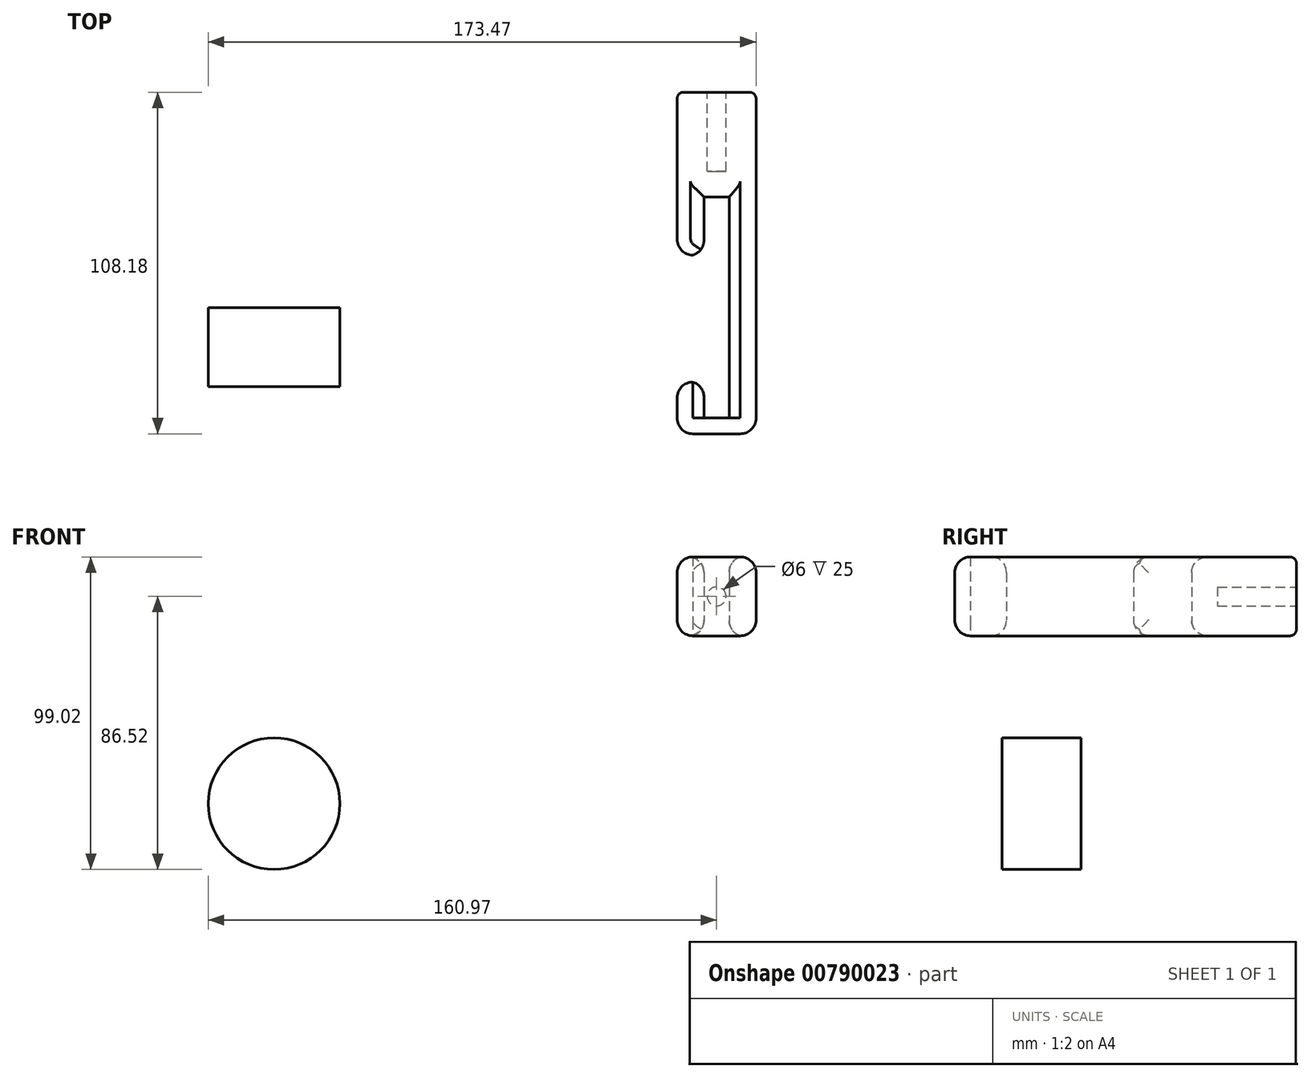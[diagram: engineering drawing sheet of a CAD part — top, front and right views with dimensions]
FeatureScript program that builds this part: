
annotation { "Feature Type Name" : "Feature", "Feature Type Description" : "" }
export const myFeature = defineFeature(function(context is Context, id is Id, definition is map)
    precondition{}
    {
        {
            var Q0;
            Q0=qCreatedBy(makeId("Top.planeOp"),FACE);
            var sketch = newSketch(context, id + "F0", { "sketchPlane" : qUnion([Q0])});
            skLineSegment(sketch, "E0.top", {"start": v(-12.5, -40) * mm, "end": v(12.5, -40) * mm});
            skLineSegment(sketch, "E0.left", {"start": v(-12.5, 40) * mm, "end": v(-12.5, 16.61) * mm});
            skLineSegment(sketch, "E0.right", {"start": v(12.5, 40) * mm, "end": v(12.5, -40) * mm});
            skPoint(sketch, "E0.middle", {"position": v(0, 0) * mm});
            skLineSegment(sketch, "E1.bottom", {"start": v(-4, 35) * mm, "end": v(4, 35) * mm});
            skLineSegment(sketch, "E1.top", {"start": v(-4, -35) * mm, "end": v(4, -35) * mm});
            skLineSegment(sketch, "E1.left", {"start": v(-4, 35) * mm, "end": v(-4, 16.61) * mm});
            skLineSegment(sketch, "E1.right", {"start": v(4, 35) * mm, "end": v(4, -35) * mm});
            skLineSegment(sketch, "E2", {"start": v(-12.5, 16.61) * mm, "end": v(-4, 16.61) * mm});
            skLineSegment(sketch, "E3", {"start": v(-12.5, -23.6) * mm, "end": v(-4, -23.6) * mm});
            skLineSegment(sketch, "E4.trimOffspring", {"start": v(-12.5, -23.6) * mm, "end": v(-12.5, -40) * mm});
            skLineSegment(sketch, "E5.trimOffspring", {"start": v(-4, -23.6) * mm, "end": v(-4, -35) * mm});
            skLineSegment(sketch, "E6.top", {"start": v(-12.5, 68.18) * mm, "end": v(12.5, 68.18) * mm});
            skLineSegment(sketch, "E7", {"start": v(-12.5, 40) * mm, "end": v(-12.5, 68.18) * mm});
            skLineSegment(sketch, "E8", {"start": v(12.5, 40) * mm, "end": v(12.5, 68.18) * mm});
            skSolve(sketch);
        }
        {
            var Q0;
            Q0 = qSketchRegion(id + "F0", true);
            extrude(context, id + "F1", {"entities" : qUnion([Q0]), "depth" : 25 * mm, "offsetDistance" : 25 * mm, "symmetric" : true});
        }
        {
            var Q0;
            Q0=makeQuery(id+"F1.opExtrude","SWEPT_FACE",FACE,{"disambiguationData":[OSD([sQuery(id+"F0.wireOp",EDGE,"E6.top")])]});
            var sketch = newSketch(context, id + "F2", { "sketchPlane" : qUnion([Q0])});
            skCircle(sketch, "E9", {"center": v(0, 0) * mm, "radius": 3 * mm});
            skSolve(sketch);
        }
        {
            var Q0;
            Q0=makeQuery(id+"F2.imprint","IMPRINT",FACE,{"disambiguationData":[TD([[makeQuery(id+"F2.imprint","IMPRINT",EDGE,{"derivedFrom":sQuery(id+"F2.wireOp",EDGE,"E9")}),1.0]])]});
            extrude(context, id + "F3", {"entities" : qUnion([Q0]), "operationType" : NewBodyOperationType.REMOVE, "oppositeDirection" : true, "depth" : 25 * mm, "offsetDistance" : 25 * mm});
        }
        {
            var Q0;
            Q0=makeQuery(id+"F1.opExtrude","SWEPT_EDGE",EDGE,{"disambiguationData":[OSD([sQuery(id+"F0.wireOp",EDGE,"E0.top"),sQuery(id+"F0.wireOp",EDGE,"E4.trimOffspring")])]});
            var Q1;
            Q1=makeQuery(id+"F1.opExtrude","SWEPT_EDGE",EDGE,{"disambiguationData":[OSD([sQuery(id+"F0.wireOp",EDGE,"E0.top"),sQuery(id+"F0.wireOp",EDGE,"E0.right")])]});
            var Q2;
            Q2=makeQuery(id+"F1.opExtrude","SWEPT_EDGE",EDGE,{"disambiguationData":[OSD([sQuery(id+"F0.wireOp",EDGE,"E3"),sQuery(id+"F0.wireOp",EDGE,"E4.trimOffspring")])]});
            var Q3;
            Q3=makeQuery(id+"F1.opExtrude","SWEPT_EDGE",EDGE,{"disambiguationData":[OSD([sQuery(id+"F0.wireOp",EDGE,"E0.left"),sQuery(id+"F0.wireOp",EDGE,"E2")])]});
            fillet(context, id + "F4", {"entities" : qUnion([Q0, Q1, Q2, Q3]), "radius" : 5 * mm, "tangentPropagation" : true, "allowEdgeOverflow" : false});
        }
        {
            var Q0;
            Q0=qCreatedBy(makeId("Front.planeOp"),FACE);
            var sketch = newSketch(context, id + "F5", { "sketchPlane" : qUnion([Q0])});
            skCircle(sketch, "E10", {"center": v(-140.12, -65.67) * mm, "radius": 20.85 * mm});
            skSolve(sketch);
        }
        {
            var Q0;
            Q0=makeQuery(id+"F5.imprint","IMPRINT",FACE,{"disambiguationData":[TD([[makeQuery(id+"F5.imprint","IMPRINT",EDGE,{"derivedFrom":sQuery(id+"F5.wireOp",EDGE,"E10")}),1.0]])]});
            extrude(context, id + "F6", {"entities" : qUnion([Q0]), "depth" : 25 * mm, "offsetDistance" : 25 * mm});
        }
        {
            var Q0;
            Q0=makeQuery(id+"F1.opExtrude","CAP_EDGE",EDGE,{"disambiguationData":[OSD([sQuery(id+"F0.wireOp",EDGE,"E6.top")])],"isStart":true});
            var Q1;
            Q1=makeQuery(id+"F1.opExtrude","SWEPT_EDGE",EDGE,{"disambiguationData":[OSD([sQuery(id+"F0.wireOp",EDGE,"E6.top"),sQuery(id+"F0.wireOp",EDGE,"E7")])]});
            var Q2;
            Q2=makeQuery(id+"F1.opExtrude","SWEPT_EDGE",EDGE,{"disambiguationData":[OSD([sQuery(id+"F0.wireOp",EDGE,"E6.top"),sQuery(id+"F0.wireOp",EDGE,"E8")])]});
            var Q3;
            Q3=makeQuery(id+"F1.opExtrude","CAP_EDGE",EDGE,{"disambiguationData":[OSD([sQuery(id+"F0.wireOp",EDGE,"E6.top")])],"isStart":false});
            fillet(context, id + "F7", {"entities" : qUnion([Q0, Q1, Q2, Q3]), "radius" : 2 * mm, "tangentPropagation" : true, "allowEdgeOverflow" : false});
        }
        {
            var Q0;
            Q0=makeQuery(id+"F1.opExtrude","CAP_EDGE",EDGE,{"disambiguationData":[OSD([sQuery(id+"F0.wireOp",EDGE,"E0.right")])],"isStart":true});
            var Q1;
            Q1=makeQuery(id+"F1.opExtrude","CAP_EDGE",EDGE,{"disambiguationData":[OSD([sQuery(id+"F0.wireOp",EDGE,"E0.right")])],"isStart":false});
            fillet(context, id + "F8", {"entities" : qUnion([Q0, Q1]), "radius" : 5 * mm, "tangentPropagation" : true, "allowEdgeOverflow" : false});
        }
        {
            var Q0;
            Q0=makeQuery(id+"F1.opExtrude","CAP_EDGE",EDGE,{"disambiguationData":[OSD([sQuery(id+"F0.wireOp",EDGE,"E1.left")])],"isStart":true});
            var Q1;
            Q1=makeQuery(id+"F1.opExtrude","CAP_EDGE",EDGE,{"disambiguationData":[OSD([sQuery(id+"F0.wireOp",EDGE,"E1.left")])],"isStart":false});
            var Q2;
            Q2=makeQuery(id+"F1.opExtrude","SWEPT_EDGE",EDGE,{"disambiguationData":[OSD([sQuery(id+"F0.wireOp",EDGE,"E1.left"),sQuery(id+"F0.wireOp",EDGE,"E2")])]});
            var Q3;
            Q3=makeQuery(id+"F1.opExtrude","SWEPT_EDGE",EDGE,{"disambiguationData":[OSD([sQuery(id+"F0.wireOp",EDGE,"E3"),sQuery(id+"F0.wireOp",EDGE,"E5.trimOffspring")])]});
            fillet(context, id + "F9", {"entities" : qUnion([Q0, Q1, Q2, Q3]), "radius" : 5 * mm, "tangentPropagation" : true, "allowEdgeOverflow" : false});
        }
        {
            var Q0;
            Q0=makeQuery(id+"F1.opExtrude","CAP_EDGE",EDGE,{"disambiguationData":[OSD([sQuery(id+"F0.wireOp",EDGE,"E0.left"),sQuery(id+"F0.wireOp",EDGE,"E7")])],"isStart":true});
            var Q1;
            Q1=makeQuery(id+"F1.opExtrude","CAP_EDGE",EDGE,{"disambiguationData":[OSD([sQuery(id+"F0.wireOp",EDGE,"E0.left"),sQuery(id+"F0.wireOp",EDGE,"E7")])],"isStart":false});
            fillet(context, id + "F10", {"entities" : qUnion([Q0, Q1]), "radius" : 5 * mm, "tangentPropagation" : true, "allowEdgeOverflow" : false});
        }
        {
            var Q0;
            Q0=makeQuery(id+"F1.opExtrude","CAP_EDGE",EDGE,{"disambiguationData":[OSD([sQuery(id+"F0.wireOp",EDGE,"E1.bottom")])],"isStart":false});
            var Q1;
            Q1=makeQuery(id+"F1.opExtrude","CAP_EDGE",EDGE,{"disambiguationData":[OSD([sQuery(id+"F0.wireOp",EDGE,"E1.bottom")])],"isStart":true});
            var Q2;
            Q2=makeQuery(id+"F1.opExtrude","CAP_EDGE",EDGE,{"disambiguationData":[OSD([sQuery(id+"F0.wireOp",EDGE,"E1.right")])],"isStart":true});
            var Q3;
            Q3=makeQuery(id+"F1.opExtrude","CAP_EDGE",EDGE,{"disambiguationData":[OSD([sQuery(id+"F0.wireOp",EDGE,"E1.right")])],"isStart":false});
            fillet(context, id + "F11", {"entities" : qUnion([Q0, Q1, Q2, Q3]), "radius" : 5 * mm, "tangentPropagation" : true, "allowEdgeOverflow" : false});
        }
    });
